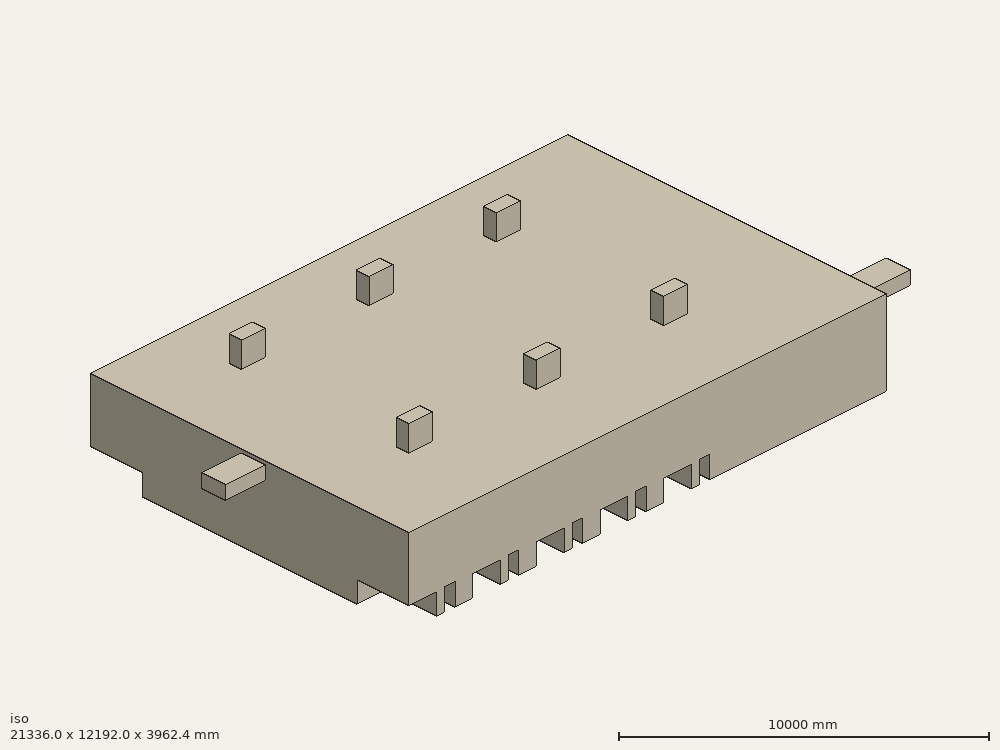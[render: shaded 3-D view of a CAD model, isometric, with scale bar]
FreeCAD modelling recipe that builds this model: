
FCSTD DOCUMENT  (FreeCAD 0.18R14555 (Git shallow))
Label: flow_domain
License: All rights reserved
LicenseURL: http://en.wikipedia.org/wiki/All_rights_reserved
objects: Part::Box×20, Part::MultiFuse×10, Part::Mirroring×1, Part::FeaturePython×1
note: 32 computed .brp shape members not serialized (recipe doc carries the construction recipe); baked Part::Feature solids carry a one-line shape summary decoded from their .brp

FEATURE [Part::Box] Box  label="Room"
  AttacherType = Attacher::AttachEngine3D
  Height = 3048
  Length = 18288
  Width = 12192
FEATURE [Part::Box] Box001  label="Bed 1"
  AttacherType = Attacher::AttachEngine3D
  Height = 762
  Length = 1066.8
  Width = 1981.2
FEATURE [Part::Box] Box002  label="Table 1"
  AttacherType = Attacher::AttachEngine3D
  Height = 798.576
  Length = 396.24
  Placement = pos=(1371.6,0,0) rot=(0,0,1;0rad)
  Width = 396.24
FEATURE [Part::MultiFuse] Fusion  label="Set 1"
  Shapes = -> [Box002,Box001]
FEATURE [Part::Box] Box003  label="Bed 002"
  AttacherType = Attacher::AttachEngine3D
  Height = 762
  Length = 1066.8
  Width = 1981.2
FEATURE [Part::Box] Box004  label="Table 002"
  AttacherType = Attacher::AttachEngine3D
  Height = 798.576
  Length = 396.24
  Placement = pos=(1371.6,0,0) rot=(0,0,1;0rad)
  Width = 396.24
FEATURE [Part::MultiFuse] Fusion001  label="Set 2"
  Placement = pos=(2438.4,0,0) rot=(0,0,1;0rad)
  Shapes = -> [Box004,Box003]
FEATURE [Part::Box] Box005  label="Table 003"
  AttacherType = Attacher::AttachEngine3D
  Height = 798.576
  Length = 396.24
  Placement = pos=(1371.6,0,0) rot=(0,0,1;0rad)
  Width = 396.24
FEATURE [Part::Box] Box006  label="Bed 003"
  AttacherType = Attacher::AttachEngine3D
  Height = 762
  Length = 1066.8
  Width = 1981.2
FEATURE [Part::MultiFuse] Fusion002  label="Set 3"
  Placement = pos=(4876.8,0,0) rot=(0,0,1;0rad)
  Shapes = -> [Box005,Box006]
FEATURE [Part::Box] Box007  label="Bed 004"
  AttacherType = Attacher::AttachEngine3D
  Height = 762
  Length = 1066.8
  Width = 1981.2
FEATURE [Part::Box] Box008  label="Table 004"
  AttacherType = Attacher::AttachEngine3D
  Height = 798.576
  Length = 396.24
  Placement = pos=(1371.6,0,0) rot=(0,0,1;0rad)
  Width = 396.24
FEATURE [Part::MultiFuse] Fusion003  label="Set 4"
  Placement = pos=(7315.2,0,0) rot=(0,0,1;0rad)
  Shapes = -> [Box008,Box007]
FEATURE [Part::Box] Box009  label="Table 005"
  AttacherType = Attacher::AttachEngine3D
  Height = 798.576
  Length = 396.24
  Placement = pos=(1371.6,0,0) rot=(0,0,1;0rad)
  Width = 396.24
FEATURE [Part::Box] Box010  label="Bed 005"
  AttacherType = Attacher::AttachEngine3D
  Height = 762
  Length = 1066.8
  Width = 1981.2
FEATURE [Part::MultiFuse] Fusion004  label="Set 5"
  Placement = pos=(9753.6,0,0) rot=(0,0,1;0rad)
  Shapes = -> [Box009,Box010]
FEATURE [Part::MultiFuse] Fusion005  label="right beds"
  Shapes = -> [Fusion001,Fusion002,Fusion003,Fusion004,Fusion]
FEATURE [Part::Mirroring] Part__Mirroring  label="left beds"
  Base = (0,6096,0)
  Normal = (0,1,0)
  Source = -> Fusion005
FEATURE [Part::Box] Box011  label="Nurse Station"
  AttacherType = Attacher::AttachEngine3D
  Height = 1219.2
  Length = 3048
  Placement = pos=(15240,7620,0) rot=(0,0,1;0rad)
  Width = 4572
FEATURE [Part::Box] Box012  label="main inlet"
  AttacherType = Attacher::AttachEngine3D
  Height = 487.68
  Length = 2438.4
  Placement = pos=(17373.6,609.6,2438.4) rot=(0,0,1;0rad)
  Width = 914.4
FEATURE [Part::Box] Box013  label="main outlet"
  AttacherType = Attacher::AttachEngine3D
  Height = 487.68
  Length = 2438.4
  Placement = pos=(-1524,5486.4,2438.4) rot=(0,0,1;0rad)
  Width = 914.4
FEATURE [Part::Box] Box014  label="branch"
  AttacherType = Attacher::AttachEngine3D
  Height = 1219.2
  Length = 914.4
  Placement = pos=(12801.6,9448.8,2743.2) rot=(0,0,1;0rad)
  Width = 487.68
FEATURE [Part::Box] Box015  label="branch001"
  AttacherType = Attacher::AttachEngine3D
  Height = 1219.2
  Length = 914.4
  Placement = pos=(12801.6,3048,2743.2) rot=(0,0,1;0rad)
  Width = 487.68
FEATURE [Part::Box] Box016  label="branch002"
  AttacherType = Attacher::AttachEngine3D
  Height = 1219.2
  Length = 914.4
  Placement = pos=(7924.8,3048,2743.2) rot=(0,0,1;0rad)
  Width = 487.68
FEATURE [Part::Box] Box017  label="branch003"
  AttacherType = Attacher::AttachEngine3D
  Height = 1219.2
  Length = 914.4
  Placement = pos=(7924.8,9448.8,2743.2) rot=(0,0,1;0rad)
  Width = 487.68
FEATURE [Part::Box] Box018  label="branch004"
  AttacherType = Attacher::AttachEngine3D
  Height = 1219.2
  Length = 914.4
  Placement = pos=(3048,3048,2743.2) rot=(0,0,1;0rad)
  Width = 487.68
FEATURE [Part::Box] Box019  label="branch005"
  AttacherType = Attacher::AttachEngine3D
  Height = 1219.2
  Length = 914.4
  Placement = pos=(3048,9448.8,2743.2) rot=(0,0,1;0rad)
  Width = 487.68
FEATURE [Part::MultiFuse] Fusion006  label="all beds"
  Shapes = -> [Part__Mirroring,Fusion005]
FEATURE [Part::FeaturePython] XOR  label="volume"  # WARN: FeaturePython — macro-defined, semantics opaque (R4)
  Objects = -> [Fusion006,Box,Box011]
  Tolerance = 0
FEATURE [Part::MultiFuse] Fusion007  label="branch ducts"
  Shapes = -> [Box019,Box016,Box018,Box017,Box015,Box014]
FEATURE [Part::MultiFuse] Fusion008  label="all vents"
  Shapes = -> [Fusion007,Box013,Box012]
FEATURE [Part::MultiFuse] Fusion009  label="flow_domain"
  Shapes = -> [Fusion008,XOR]
